# Revit family: MV8S-252(280_335_400)WV2RN1
name_source: partatom
category: Mechanical Equipment
revit_build: Autodesk Revit 2013 (Build: 20120221_2030(x64)
units: mm (PartAtom-declared; Revit-internal decimal feet)

## types (4) — shared parameters
Casing color = SB2098
Compressor = 1
Condensation = Air
Depth = 580 mm  [stored 1.90289 ft]
Description = High efficiency air cooled
Gas pipe = 25.4 mm  [stored 0.0833333 ft]
Gas pipe Radius = 12.7 mm  [stored 0.0416667 ft]
Height = 1760 mm  [stored 5.77428 ft]
Installation = Outdoor installation
Liquid pipe = 12.7 mm  [stored 0.0416667 ft]
Liquid pipe Radius = 6.35 mm  [stored 0.0208333 ft]
Power supply = 380-415V 3N~ 50Hz
Refrigerant = R410A
Series = VRF
Width = 1130 mm
clearance access behind = 300 mm
clearance access front = 1500 mm  [stored 4.92126 ft]
clearance access left = 200 mm  [stored 0.656168 ft]
clearance access right = 200 mm  [stored 0.656168 ft]

## per-type parameters (varying)
| type | Air Flow | Cooling Capacity | Cooling Power Input | Heating Capacity | Heating Power Input | Maximum Fuse Amps | Minimum Circuit Amps | Net Weight |
| 8HP | 11800.00 m³/h | 25.20 kW | 7.60 kW | 25.20 kW | 6.10 kW | 20 A | 17 A | 177.00 kg |
| 10HP | 12500.00 m³/h | 28.00 kW | 9.10 kW | 28.00 kW | 7.00 kW | 25 A | 21 A | 177.00 kg |
| 12HP | 12500.00 m³/h | 33.50 kW | 11.60 kW | 33.50 kW | 9.10 kW | 32 A | 23 A | 180.00 kg |
| 14HP | 12500.00 m³/h | 40.00 kW | 15.70 kW | 40.00 kW | 11.70 kW | 32 A | 28 A | 182.00 kg |

note: column(s) folded — value = type name in every type: Model

note: [stored X ft] marks values corroborated as IEEE doubles in the binary element streams (Revit-internal decimal feet)

## geometry (parser evidence)
native form markers: Sweep x16
no freeform markers — native parametric forms only
